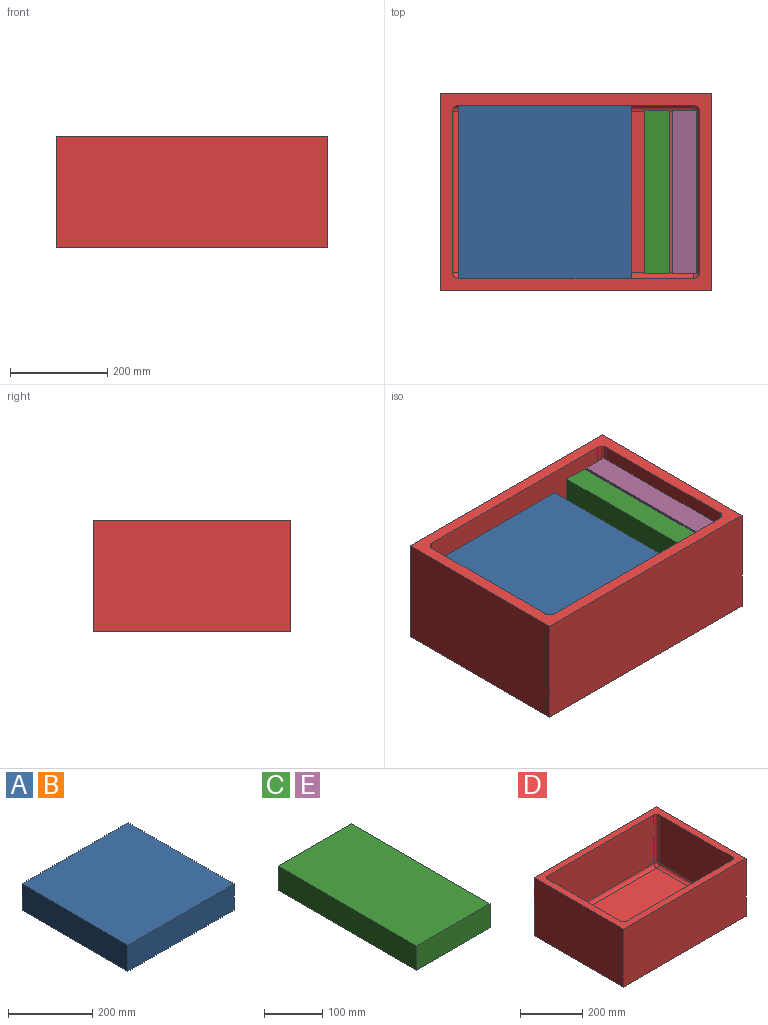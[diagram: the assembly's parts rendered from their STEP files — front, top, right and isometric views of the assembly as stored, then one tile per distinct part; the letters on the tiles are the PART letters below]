
ASSEMBLY  parts=5 mates=4
PART A: 6 faces, bbox 355.6x355.6x76.2 mm
  f0: plane 355.6x76.2mm, normal (0,1,0), area 27096.7mm2, adj f1,f3,f4,f5
  f1: plane 355.6x76.2mm, normal (-1,0,0), area 27096.7mm2, adj f0,f2,f4,f5
  f2: plane 355.6x76.2mm, normal (0,-1,0), area 27096.7mm2, adj f1,f3,f4,f5
  f3: plane 355.6x76.2mm, normal (1,0,0), area 27096.7mm2, adj f0,f2,f4,f5
  f4: plane 355.6x355.6mm, normal (0,0,1), area 126451.4mm2, adj f0,f1,f2,f3
  f5: plane 355.6x355.6mm, normal (0,0,-1), area 126451.4mm2, adj f0,f1,f2,f3
PART B: same geometry as A
PART C: 6 faces, bbox 177.8x336.6x50.8 mm
  f0: plane 336.55x50.8mm, normal (1,0,0), area 17096.7mm2, adj f1,f3,f4,f5
  f1: plane 177.8x50.8mm, normal (0,1,0), area 9032.2mm2, adj f0,f2,f4,f5
  f2: plane 336.55x50.8mm, normal (-1,0,0), area 17096.7mm2, adj f1,f3,f4,f5
  f3: plane 177.8x50.8mm, normal (0,-1,0), area 9032.2mm2, adj f0,f2,f4,f5
  f4: plane 336.55x177.8mm, normal (0,0,1), area 59838.6mm2, adj f0,f1,f2,f3
  f5: plane 336.55x177.8mm, normal (0,0,-1), area 59838.6mm2, adj f0,f1,f2,f3
PART D: 23 faces, bbox 558.8x406.4x228.6 mm
  f0: plane 558.8x406.4mm, normal (0,0,1), area 46590mm2, adj f1,f2,f3,f4,f6,f7,f8,f9
  f1: plane 558.8x228.6mm, normal (0,-1,0), area 127741.7mm2, adj f0,f2,f4,f5
  f2: plane 406.4x228.6mm, normal (1,0,0), area 92903mm2, adj f0,f1,f3,f5
  f3: plane 558.8x228.6mm, normal (0,1,0), area 127741.7mm2, adj f0,f2,f4,f5
  f4: plane 406.4x228.6mm, normal (-1,0,0), area 92903mm2, adj f0,f1,f3,f5
  f5: plane 558.8x406.4mm, normal (0,0,-1), area 227096.3mm2, adj f1,f2,f3,f4
  f6: plane 482.6x190.5mm, normal (0,1,0), area 91935.3mm2, adj f0,f11,f15,f16
  f7: plane 330.2x190.5mm, normal (-1,0,0), area 62903.1mm2, adj f0,f11,f13,f14
  f8: plane 482.6x190.5mm, normal (0,-1,0), area 91935.3mm2, adj f0,f13,f19,f22
  f9: plane 330.2x190.5mm, normal (1,0,0), area 62903.1mm2, adj f0,f16,f20,f22
  f10: plane 482.6x330.2mm, normal (0,0,1), area 159354.5mm2, adj f14,f15,f19,f20
  f11: cylinder r=12.7mm len=190.5mm, axis (0,0,-1), area 3800.3mm2, adj f0,f6,f7,f12
  f12: sphere r=12.7mm, area 253.4mm2, adj f11,f14,f15
  f13: cylinder r=12.7mm len=190.5mm, axis (0,0,1), area 3800.3mm2, adj f0,f7,f8,f17
  f14: cylinder r=12.7mm len=330.2mm, axis (0,-1,0), area 6587.2mm2, adj f7,f10,f12,f17
  f15: cylinder r=12.7mm len=482.6mm, axis (-1,0,0), area 9627.4mm2, adj f6,f10,f12,f18
  f16: cylinder r=12.7mm len=190.5mm, axis (0,0,1), area 3800.3mm2, adj f0,f6,f9,f18
  f17: sphere r=12.7mm, area 253.4mm2, adj f13,f14,f19
  f18: sphere r=12.7mm, area 253.4mm2, adj f15,f16,f20
  f19: cylinder r=12.7mm len=482.6mm, axis (1,0,0), area 9627.4mm2, adj f8,f10,f17,f21
  f20: cylinder r=12.7mm len=330.2mm, axis (0,1,0), area 6587.2mm2, adj f9,f10,f18,f21
  f21: sphere r=12.7mm, area 253.4mm2, adj f19,f20,f22
  f22: cylinder r=12.7mm len=190.5mm, axis (0,0,-1), area 3800.3mm2, adj f0,f8,f9,f21
PART E: same geometry as C
PLACE A rot(axis=(1,0,0),180deg) t=(-62.74,0,152.4)mm
PLACE B t=(-62.74,0,0)mm
PLACE C rot(axis=(0,-1,0),90deg) t=(192.53,0,-292.1)mm
PLACE D at identity fixed
PLACE E rot(axis=(-0.71,0,0.71),180deg) t=(248.16,0,469.9)mm
MATE planar B.f4 <-> A.f4  axis (0,0,1) through (-62.74,0,76.2)mm
MATE planar D.f10 <-> E.f0  axis (0,0,1) through (0,0,0)mm
MATE planar D.f10 <-> B.f5  axis (0,0,1) through (0,0,0)mm
MATE planar D.f10 <-> C.f2  axis (0,0,1) through (0,0,0)mm
